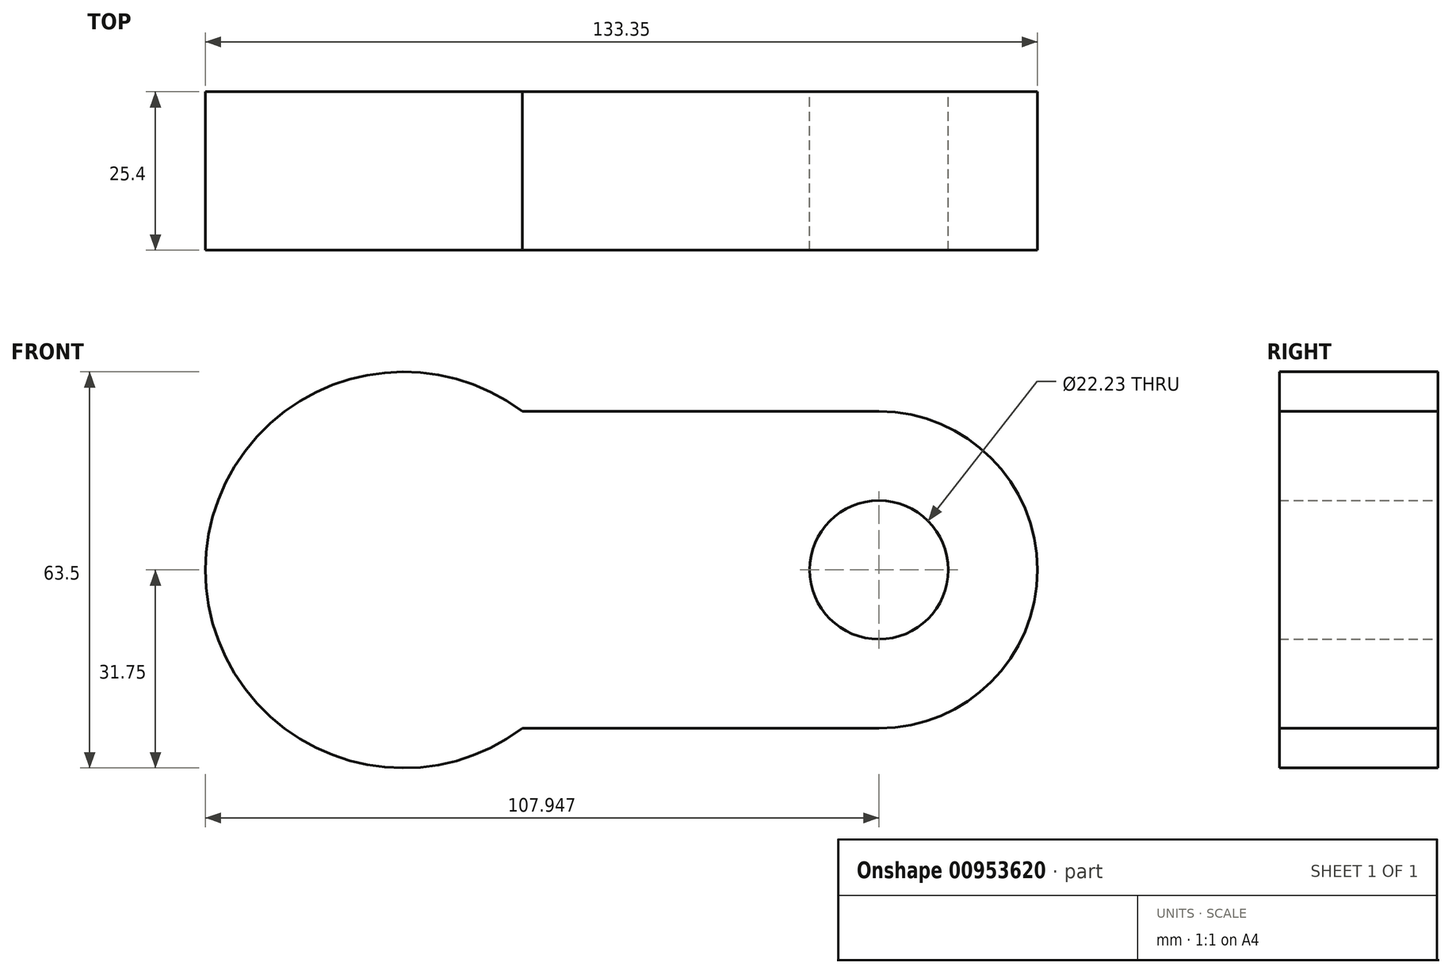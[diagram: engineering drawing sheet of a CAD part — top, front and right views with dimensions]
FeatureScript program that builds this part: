
annotation { "Feature Type Name" : "Feature", "Feature Type Description" : "" }
export const myFeature = defineFeature(function(context is Context, id is Id, definition is map)
    precondition{}
    {
        {
            var Q0;
            Q0=qCreatedBy(makeId("Front.planeOp"),FACE);
            var sketch = newSketch(context, id + "F0", { "sketchPlane" : qUnion([Q0])});
            skCircle(sketch, "E0", {"center": v(-44.54, 0) * mm, "radius": 31.75 * mm});
            skArc(sketch, "E1", {"start": v(31.66, -25.4) * mm, "mid": v(57.06, 0) * mm, "end": v(31.66, 25.4) * mm});
            skLineSegment(sketch, "E2", {"start": v(31.66, 25.4) * mm, "end": v(-25.5, 25.4) * mm});
            skLineSegment(sketch, "E3", {"start": v(31.66, -25.4) * mm, "end": v(-25.5, -25.4) * mm});
            skCircle(sketch, "E4", {"center": v(31.66, 0) * mm, "radius": 11.11 * mm});
            skLineSegment(sketch, "E5.bottom", {"start": v(-29.34, 4.56) * mm, "end": v(-24.58, 4.56) * mm});
            skLineSegment(sketch, "E5.top", {"start": v(-29.34, -4.96) * mm, "end": v(-24.58, -4.96) * mm});
            skLineSegment(sketch, "E5.right", {"start": v(-24.58, 4.56) * mm, "end": v(-24.58, -4.96) * mm});
            skArc(sketch, "E6", {"start": v(-29.34, 4.56) * mm, "mid": v(-60.42, 0.2) * mm, "end": v(-29.46, -4.96) * mm});
            skSolve(sketch);
        }
        {
            var Q0;
            Q0 = qSketchRegion(id + "F0", true);
            extrude(context, id + "F1", {"entities" : qUnion([Q0]), "depth" : 25.4 * mm, "offsetDistance" : 25.4 * mm});
        }
    });
